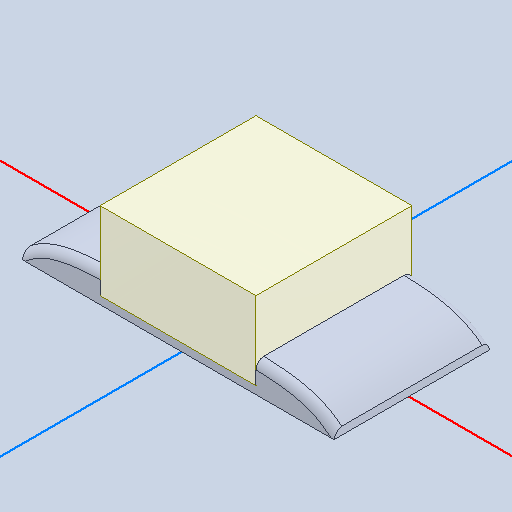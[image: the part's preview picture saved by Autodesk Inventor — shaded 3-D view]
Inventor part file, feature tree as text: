
AUTODESK INVENTOR PART (.ipt)
format: ipt  version: 2022 (Build 260153000, 153)  size: 134,144 bytes
history: native  units: mm
features: other x3, fillet x1
ambient origin geometry x8: Origin, YZ Plane, XZ Plane, XY Plane, X Axis, Y Axis, Z Axis, Center Point
bodies: Body1 (feature_tree), Body2 (feature_tree)
feature tree (4):
  other  "Твердое тело1"
  other  "Твердое тело2"
  other  "Boss-Extrude1"
  fillet  "Fillet1"  [1 undecoded]
note: 1 required parameter value undecoded (feature->parameter linkage not recoverable at this tier; creation-order binding heuristic only, values carry confidence <= 0.55)
